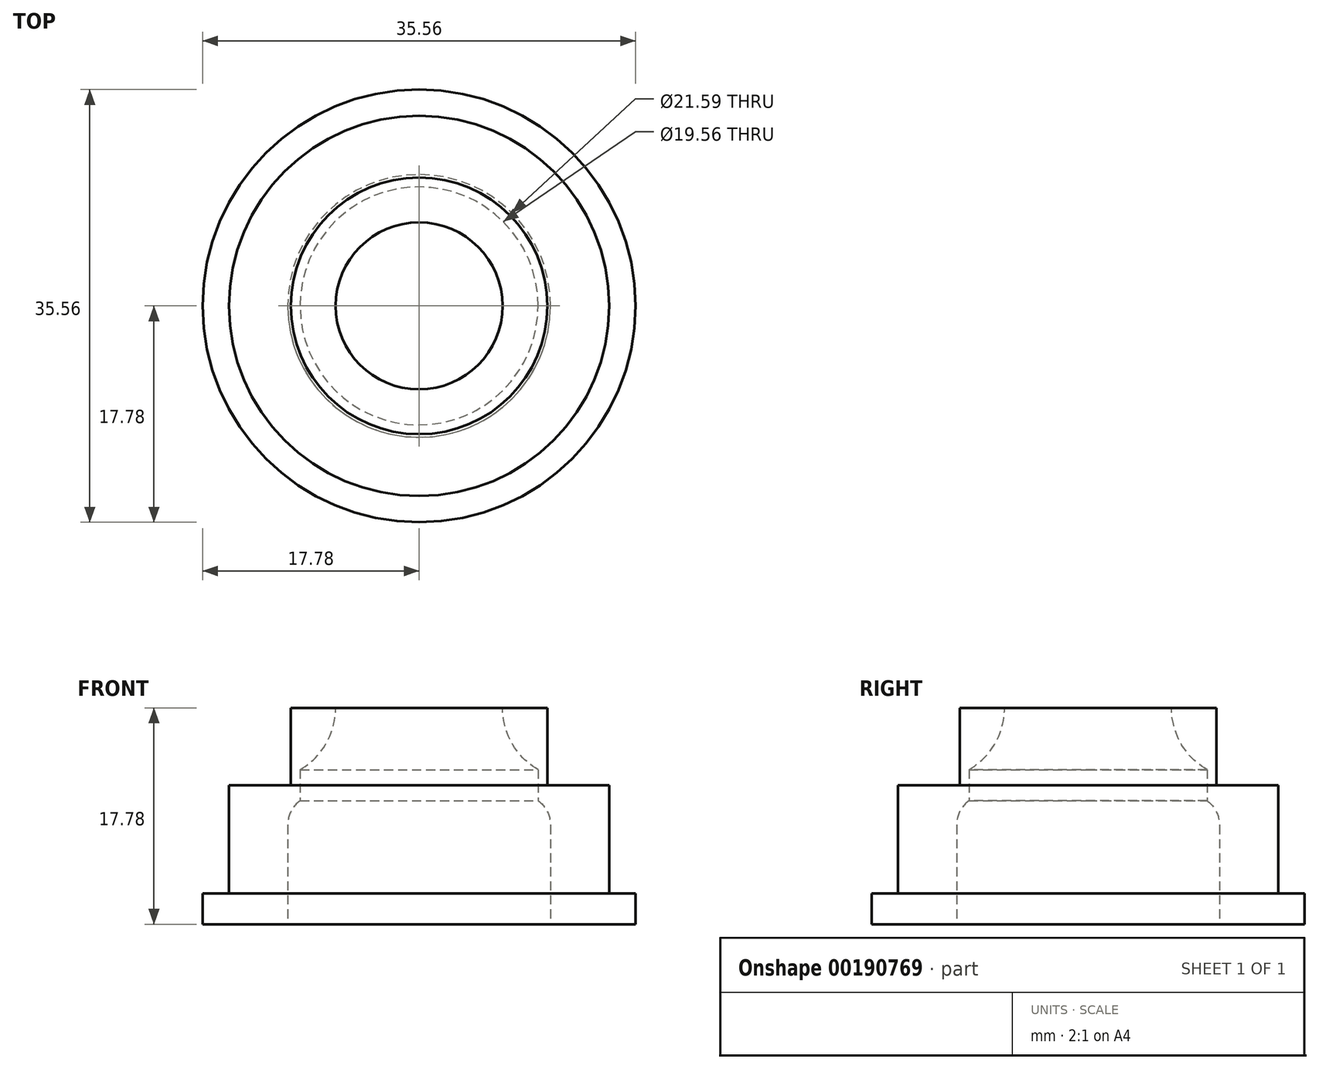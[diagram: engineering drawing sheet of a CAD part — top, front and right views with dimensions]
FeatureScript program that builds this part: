
annotation { "Feature Type Name" : "Feature", "Feature Type Description" : "" }
export const myFeature = defineFeature(function(context is Context, id is Id, definition is map)
    precondition{}
    {
        {
            var Q0;
            Q0=qCreatedBy(makeId("Top.planeOp"),FACE);
            var sketch = newSketch(context, id + "F0", { "sketchPlane" : qUnion([Q0])});
            skCircle(sketch, "E0", {"center": v(0, 0) * mm, "radius": 15.62 * mm});
            skSolve(sketch);
        }
        {
            var Q0;
            Q0 = qSketchRegion(id + "F0", true);
            extrude(context, id + "F1", {"entities" : qUnion([Q0]), "depth" : 11.43 * mm});
        }
        {
            var Q0;
            Q0=makeQuery(id+"F1.opExtrude","CAP_FACE",FACE,{"disambiguationData":[OSD([sQuery(id+"F0.wireOp",EDGE,"E0")])],"isStart":false});
            var sketch = newSketch(context, id + "F2", { "sketchPlane" : qUnion([Q0])});
            skCircle(sketch, "E1", {"center": v(0, 0) * mm, "radius": 10.54 * mm});
            skSolve(sketch);
        }
        {
            var Q0;
            Q0 = qSketchRegion(id + "F2", true);
            extrude(context, id + "F3", {"entities" : qUnion([Q0]), "operationType" : NewBodyOperationType.ADD, "depth" : 6.35 * mm});
        }
        {
            var Q0;
            Q0=makeQuery(id+"F1.opExtrude","CAP_FACE",FACE,{"disambiguationData":[OSD([sQuery(id+"F0.wireOp",EDGE,"E0")])],"isStart":true});
            var sketch = newSketch(context, id + "F4", { "sketchPlane" : qUnion([Q0])});
            skCircle(sketch, "E2", {"center": v(0, 0) * mm, "radius": 17.78 * mm});
            skSolve(sketch);
        }
        {
            var Q0;
            Q0 = qSketchRegion(id + "F4", true);
            extrude(context, id + "F5", {"entities" : qUnion([Q0]), "operationType" : NewBodyOperationType.ADD, "oppositeDirection" : true, "depth" : 2.54 * mm});
        }
        {
            var Q0;
            Q0=makeQuery(id+"F3.opExtrude","CAP_FACE",FACE,{"disambiguationData":[OSD([sQuery(id+"F2.wireOp",EDGE,"E1")])],"isStart":false});
            var sketch = newSketch(context, id + "F6", { "sketchPlane" : qUnion([Q0])});
            skCircle(sketch, "E3", {"center": v(0, 0) * mm, "radius": 6.67 * mm});
            skSolve(sketch);
        }
        {
            var Q0;
            Q0 = qSketchRegion(id + "F6", true);
            extrude(context, id + "F7", {"entities" : qUnion([Q0]), "operationType" : NewBodyOperationType.REMOVE, "endBound" : BoundingType.THROUGH_ALL, "oppositeDirection" : true, "depth" : 25.4 * mm});
        }
        {
            var Q0;
            Q0=qCreatedBy(makeId("Front.planeOp"),FACE);
            var sketch = newSketch(context, id + "F8", { "sketchPlane" : qUnion([Q0])});
            skPoint(sketch, "E4", {"position": v(6.86, 17.78) * mm});
            skPoint(sketch, "E5", {"position": v(0, 17.78) * mm});
            skLineSegment(sketch, "E6", {"start": v(6.86, 17.78) * mm, "end": v(6.86, 12.7) * mm, "construction": true});
            skPoint(sketch, "E7", {"position": v(9.78, 12.7) * mm});
            skLineSegment(sketch, "E8", {"start": v(6.86, 17.78) * mm, "end": v(6.86, 23.37) * mm, "construction": true});
            skArc(sketch, "E9", {"start": v(6.86, 17.78) * mm, "mid": v(7.64, 14.85) * mm, "end": v(9.78, 12.7) * mm});
            skLineSegment(sketch, "E10", {"start": v(6.86, 17.78) * mm, "end": v(1.04, 17.78) * mm});
            skLineSegment(sketch, "E11", {"start": v(1.04, 17.78) * mm, "end": v(1.04, -3.8) * mm});
            skLineSegment(sketch, "E12", {"start": v(9.78, 12.7) * mm, "end": v(9.78, 10.16) * mm});
            skPoint(sketch, "E13", {"position": v(10.8, 8.13) * mm});
            skArc(sketch, "E14", {"start": v(10.8, 8.13) * mm, "mid": v(10.53, 9.26) * mm, "end": v(9.78, 10.16) * mm});
            skLineSegment(sketch, "E15", {"start": v(9.78, 10.16) * mm, "end": v(6.84, 10.16) * mm, "construction": true});
            skLineSegment(sketch, "E16", {"start": v(10.8, 8.13) * mm, "end": v(10.8, -3.8) * mm});
            skLineSegment(sketch, "E17", {"start": v(10.8, -3.8) * mm, "end": v(1.04, -3.8) * mm});
            skLineSegment(sketch, "E18", {"start": v(0, 17.78) * mm, "end": v(0, -16.3) * mm, "construction": true});
            skSolve(sketch);
        }
        {
            var Q0;
            Q0 = qSketchRegion(id + "F8", true);
            var Q1;
            Q1=sQuery(id+"F8.wireOp",EDGE,"E18");
            revolve(context, id + "F9", {"operationType" : NewBodyOperationType.REMOVE, "entities" : qUnion([Q0]), "axis" : qUnion([Q1]), "revolveType" : RevolveType.FULL, "oppositeDirection" : true});
        }
    });
